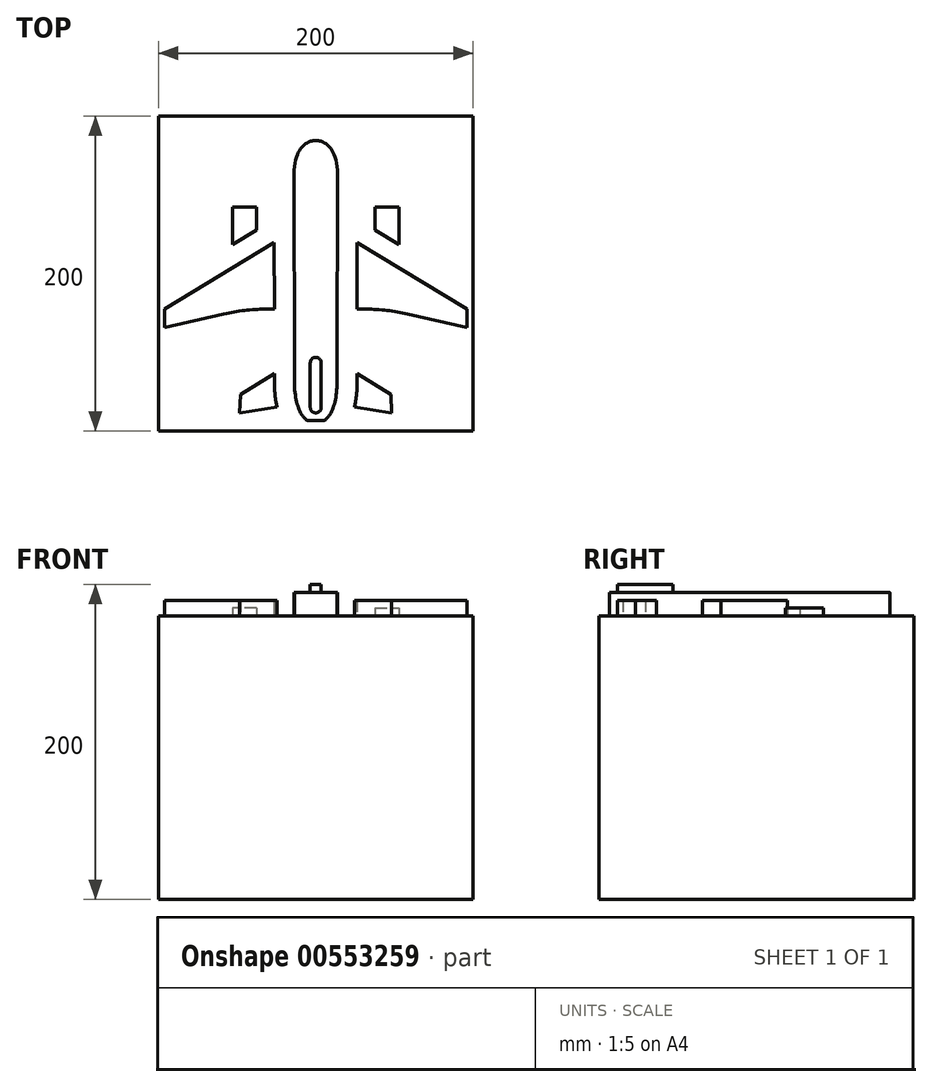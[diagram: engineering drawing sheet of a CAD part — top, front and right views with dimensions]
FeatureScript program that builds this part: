
annotation { "Feature Type Name" : "Feature", "Feature Type Description" : "" }
export const myFeature = defineFeature(function(context is Context, id is Id, definition is map)
    precondition{}
    {
        {
            var Q0;
            Q0=qCreatedBy(makeId("Top.planeOp"),FACE);
            var sketch = newSketch(context, id + "F0", { "sketchPlane" : qUnion([Q0])});
            skLineSegment(sketch, "E0.bottom", {"start": v(100, 100) * mm, "end": v(-100, 100) * mm});
            skLineSegment(sketch, "E0.top", {"start": v(100, -100) * mm, "end": v(-100, -100) * mm});
            skLineSegment(sketch, "E0.left", {"start": v(100, 100) * mm, "end": v(100, -100) * mm});
            skLineSegment(sketch, "E0.right", {"start": v(-100, 100) * mm, "end": v(-100, -100) * mm});
            skPoint(sketch, "E0.middle", {"position": v(0, 0) * mm});
            skLineSegment(sketch, "E1.right", {"start": v(-13.74, 63.14) * mm, "end": v(-13.45, -60.55) * mm});
            skPoint(sketch, "E1.middle", {"position": v(0, 4.29) * mm});
            skPoint(sketch, "E2.endSnap0", {"position": v(0, -77.1) * mm});
            skLineSegment(sketch, "E3", {"start": v(-4.38, -93.4) * mm, "end": v(0, -93.4) * mm});
            skFitSpline(sketch, "E4", {"points": [v(-13.43, -70.57) * mm, v(-4.38, -93.4) * mm], "startDerivative": vector(-0.07, -39.95) * mm, "endDerivative": vector(10.87, 0) * mm});
            skPoint(sketch, "E2.start.orphan", {"position": v(0, -77.24) * mm});
            skLineSegment(sketch, "E5", {"start": v(-26.35, 19.69) * mm, "end": v(-96.1, -22.66) * mm});
            skLineSegment(sketch, "E6", {"start": v(-96.1, -22.66) * mm, "end": v(-96.07, -34.43) * mm});
            skLineSegment(sketch, "E7", {"start": v(-96.07, -34.43) * mm, "end": v(-58.4, -25.68) * mm});
            skLineSegment(sketch, "E8", {"start": v(-31.98, -22.66) * mm, "end": v(-26.24, -22.66) * mm});
            skLineSegment(sketch, "E9", {"start": v(-26.14, -63.54) * mm, "end": v(-47.9, -76.9) * mm});
            skLineSegment(sketch, "E10", {"start": v(-47.9, -76.9) * mm, "end": v(-48.23, -88.43) * mm});
            skLineSegment(sketch, "E11", {"start": v(-48.23, -88.43) * mm, "end": v(-24.4, -84.85) * mm});
            skPoint(sketch, "E12.orphan", {"position": v(0, 35.68) * mm});
            skPoint(sketch, "E13.orphan", {"position": v(0, -22.66) * mm});
            skPoint(sketch, "E14.orphan", {"position": v(0, -47.48) * mm});
            skPoint(sketch, "E15.orphan", {"position": v(0, -81.18) * mm});
            skLineSegment(sketch, "E16.2", {"start": v(-26.35, 19.69) * mm, "end": v(-26.24, -22.66) * mm});
            skFitSpline(sketch, "E16.3", {"points": [v(-26.13, -70.55) * mm, v(-26.13, -72.64) * mm, v(-25.92, -76.71) * mm, v(-25.06, -82.37) * mm, v(-23.71, -87.55) * mm, v(-22.23, -91.46) * mm, v(-20.82, -94.36) * mm, v(-19.63, -96.44) * mm, v(-18.28, -98.43) * mm, v(-16.7, -100.35) * mm, v(-15.1, -101.9) * mm, v(-13.54, -103.1) * mm, v(-12.2, -103.97) * mm, v(-10.64, -104.77) * mm, v(-8.83, -105.46) * mm, v(-6.75, -105.96) * mm, v(-5.2, -106.1) * mm, v(-4.38, -106.1) * mm]});
            skLineSegment(sketch, "E17.bottom", {"start": v(-37.74, 42.3) * mm, "end": v(-53, 42.3) * mm});
            skLineSegment(sketch, "E17.left", {"start": v(-37.74, 42.3) * mm, "end": v(-37.74, 27.63) * mm});
            skLineSegment(sketch, "E17.right", {"start": v(-53, 42.3) * mm, "end": v(-53, 18.37) * mm});
            skPoint(sketch, "E17.middle", {"position": v(-45.37, 20.57) * mm});
            skLineSegment(sketch, "E18", {"start": v(-13.45, -60.55) * mm, "end": v(-13.43, -70.57) * mm});
            skPoint(sketch, "E19", {"position": v(0, 84.6) * mm});
            skPoint(sketch, "E20", {"position": v(0, 109.75) * mm});
            skLineSegment(sketch, "E21.trimOffspring", {"start": v(-37.74, 27.63) * mm, "end": v(-53, 18.37) * mm});
            skLineSegment(sketch, "E22.trimOffspring", {"start": v(-26.14, -63.54) * mm, "end": v(-26.13, -70.55) * mm});
            skPoint(sketch, "E17.top.start.orphan", {"position": v(-37.74, -1.16) * mm});
            skPoint(sketch, "E23.trimOffspring.end.orphan", {"position": v(-53, -1.16) * mm});
            skFitSpline(sketch, "E24", {"points": [v(0, 84.6) * mm, v(-13.74, 63.14) * mm], "startDerivative": vector(-6.1, 0) * mm, "endDerivative": vector(0, -60.94) * mm});
            skLineSegment(sketch, "E25.MirrorCS", {"start": v(13.74, 63.14) * mm, "end": v(13.45, -60.55) * mm});
            skFitSpline(sketch, "E26.MirrorCS", {"points": [v(0, 84.6) * mm, v(13.74, 63.14) * mm], "startDerivative": vector(6.1, 0) * mm, "endDerivative": vector(0, -60.94) * mm});
            skFitSpline(sketch, "E27.MirrorCS", {"points": [v(13.43, -70.57) * mm, v(4.38, -93.4) * mm], "startDerivative": vector(0.07, -39.95) * mm, "endDerivative": vector(-10.87, 0) * mm});
            skLineSegment(sketch, "E28.MirrorCS", {"start": v(4.38, -93.4) * mm, "end": v(0, -93.4) * mm});
            skLineSegment(sketch, "E29.MirrorCS", {"start": v(13.45, -60.55) * mm, "end": v(13.43, -70.57) * mm});
            skLineSegment(sketch, "E30.MirrorCS", {"start": v(26.14, -63.54) * mm, "end": v(47.9, -76.9) * mm});
            skLineSegment(sketch, "E31.MirrorCS", {"start": v(26.14, -63.54) * mm, "end": v(26.13, -70.55) * mm});
            skFitSpline(sketch, "E32.MirrorCS", {"points": [v(26.13, -70.55) * mm, v(26.13, -72.64) * mm, v(25.92, -76.71) * mm, v(25.06, -82.37) * mm, v(23.71, -87.55) * mm, v(22.23, -91.46) * mm, v(20.82, -94.36) * mm, v(19.63, -96.44) * mm, v(18.28, -98.43) * mm, v(16.7, -100.35) * mm, v(15.1, -101.9) * mm, v(13.54, -103.1) * mm, v(12.2, -103.97) * mm, v(10.64, -104.77) * mm, v(8.83, -105.46) * mm, v(6.75, -105.96) * mm, v(5.2, -106.1) * mm, v(4.38, -106.1) * mm]});
            skLineSegment(sketch, "E33.MirrorCS", {"start": v(48.23, -88.43) * mm, "end": v(24.4, -84.85) * mm});
            skLineSegment(sketch, "E34.MirrorCS", {"start": v(47.9, -76.9) * mm, "end": v(48.23, -88.43) * mm});
            skLineSegment(sketch, "E35.MirrorCS", {"start": v(37.74, 27.63) * mm, "end": v(53, 18.37) * mm});
            skLineSegment(sketch, "E36.MirrorCS", {"start": v(53, 42.3) * mm, "end": v(53, 18.37) * mm});
            skLineSegment(sketch, "E37.MirrorCS", {"start": v(37.74, 42.3) * mm, "end": v(53, 42.3) * mm});
            skLineSegment(sketch, "E38.MirrorCS", {"start": v(37.74, 42.3) * mm, "end": v(37.74, 27.63) * mm});
            skLineSegment(sketch, "E39.MirrorCS", {"start": v(26.35, 19.69) * mm, "end": v(96.1, -22.66) * mm});
            skLineSegment(sketch, "E40.MirrorCS", {"start": v(26.35, 19.69) * mm, "end": v(26.24, -22.66) * mm});
            skLineSegment(sketch, "E41.MirrorCS", {"start": v(31.98, -22.66) * mm, "end": v(26.24, -22.66) * mm});
            skLineSegment(sketch, "E42.MirrorCS", {"start": v(96.07, -34.43) * mm, "end": v(58.4, -25.68) * mm});
            skLineSegment(sketch, "E43", {"start": v(96.1, -22.66) * mm, "end": v(96.07, -34.43) * mm});
            skPoint(sketch, "E44.visualSharp", {"position": v(-45.37, -22.66) * mm});
            skArc(sketch, "E44.filletArc", {"start": v(-31.98, -22.66) * mm, "mid": v(-45.28, -23.41) * mm, "end": v(-58.4, -25.68) * mm});
            skPoint(sketch, "E45.visualSharp", {"position": v(45.37, -22.66) * mm});
            skArc(sketch, "E45.filletArc", {"start": v(58.4, -25.68) * mm, "mid": v(45.28, -23.41) * mm, "end": v(31.98, -22.66) * mm});
            skSolve(sketch);
        }
        {
            var Q0;
            Q0=makeQuery(id+"F0.imprint","IMPRINT",FACE,{"disambiguationData":[TD([[makeQuery(id+"F0.imprint","IMPRINT",EDGE,{"derivedFrom":sQuery(id+"F0.wireOp",EDGE,"E0.bottom")}),1.0]])]});
            var Q1;
            Q1=makeQuery(id+"F0.imprint","IMPRINT",FACE,{"disambiguationData":[TD([[makeQuery(id+"F0.imprint","IMPRINT",EDGE,{"derivedFrom":sQuery(id+"F0.wireOp",EDGE,"E17.bottom")}),1.0]])]});
            var Q2;
            Q2=makeQuery(id+"F0.imprint","IMPRINT",FACE,{"disambiguationData":[TD([[makeQuery(id+"F0.imprint","IMPRINT",EDGE,{"derivedFrom":sQuery(id+"F0.wireOp",EDGE,"E1.right")}),1.0]])]});
            var Q3;
            Q3=makeQuery(id+"F0.imprint","IMPRINT",FACE,{"disambiguationData":[TD([[makeQuery(id+"F0.imprint","IMPRINT",EDGE,{"derivedFrom":sQuery(id+"F0.wireOp",EDGE,"E5")}),1.0]])]});
            var Q4;
            Q4=makeQuery(id+"F0.imprint","IMPRINT",FACE,{"disambiguationData":[TD([[makeQuery(id+"F0.imprint","IMPRINT",EDGE,{"derivedFrom":sQuery(id+"F0.wireOp",EDGE,"E39.MirrorCS")}),-1.0]])]});
            var Q5;
            Q5=makeQuery(id+"F0.imprint","IMPRINT",FACE,{"disambiguationData":[TD([[makeQuery(id+"F0.imprint","IMPRINT",EDGE,{"derivedFrom":sQuery(id+"F0.wireOp",EDGE,"E35.MirrorCS")}),1.0]])]});
            var Q6;
            Q6=makeQuery(id+"F0.imprint","IMPRINT",FACE,{"disambiguationData":[TD([[makeQuery(id+"F0.imprint","IMPRINT",EDGE,{"derivedFrom":sQuery(id+"F0.wireOp",EDGE,"E30.MirrorCS")}),-1.0]])]});
            var Q7;
            Q7=makeQuery(id+"F0.imprint","IMPRINT",FACE,{"disambiguationData":[TD([[makeQuery(id+"F0.imprint","IMPRINT",EDGE,{"derivedFrom":sQuery(id+"F0.wireOp",EDGE,"E9")}),1.0]])]});
            extrude(context, id + "F1", {"entities" : qUnion([Q0, Q1, Q2, Q3, Q4, Q5, Q6, Q7]), "depth" : 180 * mm, "offsetDistance" : 25 * mm});
        }
        {
            var Q0;
            Q0=makeQuery(id+"F0.imprint","IMPRINT",FACE,{"disambiguationData":[TD([[makeQuery(id+"F0.imprint","IMPRINT",EDGE,{"derivedFrom":sQuery(id+"F0.wireOp",EDGE,"E1.right")}),1.0]])]});
            var Q1;
            Q1=makeQuery(id+"F0.imprint","IMPRINT",FACE,{"disambiguationData":[TD([[makeQuery(id+"F0.imprint","IMPRINT",EDGE,{"derivedFrom":sQuery(id+"F0.wireOp",EDGE,"E5")}),1.0]])]});
            var Q2;
            Q2=makeQuery(id+"F0.imprint","IMPRINT",FACE,{"disambiguationData":[TD([[makeQuery(id+"F0.imprint","IMPRINT",EDGE,{"derivedFrom":sQuery(id+"F0.wireOp",EDGE,"E9")}),1.0]])]});
            var Q3;
            Q3=makeQuery(id+"F0.imprint","IMPRINT",FACE,{"disambiguationData":[TD([[makeQuery(id+"F0.imprint","IMPRINT",EDGE,{"derivedFrom":sQuery(id+"F0.wireOp",EDGE,"E30.MirrorCS")}),-1.0]])]});
            var Q4;
            Q4=makeQuery(id+"F0.imprint","IMPRINT",FACE,{"disambiguationData":[TD([[makeQuery(id+"F0.imprint","IMPRINT",EDGE,{"derivedFrom":sQuery(id+"F0.wireOp",EDGE,"E39.MirrorCS")}),-1.0]])]});
            var Q5;
            Q5=makeQuery(id+"F0.imprint","IMPRINT",FACE,{"disambiguationData":[TD([[makeQuery(id+"F0.imprint","IMPRINT",EDGE,{"derivedFrom":sQuery(id+"F0.wireOp",EDGE,"E35.MirrorCS")}),1.0]])]});
            var Q6;
            Q6=makeQuery(id+"F0.imprint","IMPRINT",FACE,{"disambiguationData":[TD([[makeQuery(id+"F0.imprint","IMPRINT",EDGE,{"derivedFrom":sQuery(id+"F0.wireOp",EDGE,"E17.bottom")}),1.0]])]});
            extrude(context, id + "F2", {"entities" : qUnion([Q0, Q1, Q2, Q3, Q4, Q5, Q6]), "operationType" : NewBodyOperationType.ADD, "depth" : 185 * mm, "offsetDistance" : 25 * mm});
        }
        {
            var Q0;
            Q0=makeQuery(id+"F0.imprint","IMPRINT",FACE,{"disambiguationData":[TD([[makeQuery(id+"F0.imprint","IMPRINT",EDGE,{"derivedFrom":sQuery(id+"F0.wireOp",EDGE,"E1.right")}),1.0]])]});
            var Q1;
            Q1=makeQuery(id+"F0.imprint","IMPRINT",FACE,{"disambiguationData":[TD([[makeQuery(id+"F0.imprint","IMPRINT",EDGE,{"derivedFrom":sQuery(id+"F0.wireOp",EDGE,"E5")}),1.0]])]});
            var Q2;
            Q2=makeQuery(id+"F0.imprint","IMPRINT",FACE,{"disambiguationData":[TD([[makeQuery(id+"F0.imprint","IMPRINT",EDGE,{"derivedFrom":sQuery(id+"F0.wireOp",EDGE,"E9")}),1.0]])]});
            var Q3;
            Q3=makeQuery(id+"F0.imprint","IMPRINT",FACE,{"disambiguationData":[TD([[makeQuery(id+"F0.imprint","IMPRINT",EDGE,{"derivedFrom":sQuery(id+"F0.wireOp",EDGE,"E30.MirrorCS")}),-1.0]])]});
            var Q4;
            Q4=makeQuery(id+"F0.imprint","IMPRINT",FACE,{"disambiguationData":[TD([[makeQuery(id+"F0.imprint","IMPRINT",EDGE,{"derivedFrom":sQuery(id+"F0.wireOp",EDGE,"E39.MirrorCS")}),-1.0]])]});
            extrude(context, id + "F3", {"entities" : qUnion([Q0, Q1, Q2, Q3, Q4]), "operationType" : NewBodyOperationType.ADD, "depth" : 190 * mm, "offsetDistance" : 25 * mm});
        }
        {
            var Q0;
            Q0=makeQuery(id+"F0.imprint","IMPRINT",FACE,{"disambiguationData":[TD([[makeQuery(id+"F0.imprint","IMPRINT",EDGE,{"derivedFrom":sQuery(id+"F0.wireOp",EDGE,"E1.right")}),1.0]])]});
            extrude(context, id + "F4", {"entities" : qUnion([Q0]), "operationType" : NewBodyOperationType.ADD, "depth" : 195 * mm, "offsetDistance" : 25 * mm});
        }
        {
            var Q0;
            Q0=makeQuery(id+"F4.opExtrude","CAP_FACE",FACE,{"disambiguationData":[OSD([sQuery(id+"F0.wireOp",EDGE,"E1.right"),sQuery(id+"F0.wireOp",EDGE,"E3"),sQuery(id+"F0.wireOp",EDGE,"E4"),sQuery(id+"F0.wireOp",EDGE,"E18"),sQuery(id+"F0.wireOp",EDGE,"E24"),sQuery(id+"F0.wireOp",EDGE,"E25.MirrorCS"),sQuery(id+"F0.wireOp",EDGE,"E26.MirrorCS"),sQuery(id+"F0.wireOp",EDGE,"E27.MirrorCS"),sQuery(id+"F0.wireOp",EDGE,"E28.MirrorCS"),sQuery(id+"F0.wireOp",EDGE,"E29.MirrorCS")])],"isStart":false});
            var sketch = newSketch(context, id + "F5", { "sketchPlane" : qUnion([Q0])});
            skLineSegment(sketch, "E46.left", {"start": v(3.5, -56.71) * mm, "end": v(3.5, -84.98) * mm});
            skLineSegment(sketch, "E46.right", {"start": v(-3.5, -56.71) * mm, "end": v(-3.5, -84.98) * mm});
            skArc(sketch, "E47", {"start": v(3.5, -56.71) * mm, "mid": v(0, -53.22) * mm, "end": v(-3.5, -56.71) * mm});
            skArc(sketch, "E48", {"start": v(-3.5, -84.98) * mm, "mid": v(0, -88.47) * mm, "end": v(3.5, -84.98) * mm});
            skSolve(sketch);
        }
        {
            var Q0;
            Q0=makeQuery(id+"F5.imprint","IMPRINT",FACE,{"disambiguationData":[TD([[makeQuery(id+"F5.imprint","IMPRINT",EDGE,{"derivedFrom":sQuery(id+"F5.wireOp",EDGE,"E46.left")}),-1.0]])]});
            extrude(context, id + "F6", {"entities" : qUnion([Q0]), "operationType" : NewBodyOperationType.ADD, "depth" : 5 * mm, "offsetDistance" : 25 * mm});
        }
    });
